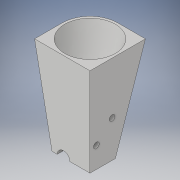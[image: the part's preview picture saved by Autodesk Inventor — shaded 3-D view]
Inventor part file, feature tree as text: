
AUTODESK INVENTOR PART (.ipt)
format: ipt  version: 2018 (Build 220112000, 112)  size: 186,368 bytes
history: native  units: in
note: dims shown in document units (in); Inventor stores cm internally (conversion verified against a paired STEP export)
features: sketch x6, loft x2, extrude x2, plane x1
ambient origin geometry x8: Origin, YZ Plane, XZ Plane, XY Plane, X Axis, Y Axis, Z Axis, Center Point
bodies: Solid1 (feature_tree)
feature tree (11):
  sketch  "Sketch1"  dims[d1=0.8in d2=1.2in]
  plane  "Work Plane1"
  loft  "Loft1"
  loft  "Loft2"
  extrude  "Extrusion1"  Depth=0.875in
  extrude  "Extrusion3"  TaperAngle=0.0deg  [1 undecoded]
  sketch  "Sketch3"  dims[d4=0.4in d5=2.8in]
  sketch  "Sketch4"  dims[d15=0.875in d17=0.875in]
  sketch  "Sketch5"  dims[d18=0.875in d19=0.0in d20=90.0deg]
  sketch  "Sketch6"  dims[d21=0.0in d22=90.0deg]
  sketch  "Sketch8"  dims[d23=1.6in d24=0.875in d26=0.875in d27=0.65in d28=0.0in d29=90.0deg d30=0.0in d31=90.0deg d32=0.4in d33=0.4in d34=0.4in d35=0.2in d36=0.0in d38=3.0in d39=0.0in d42=0.0in d43=0.25in d44=0.32in d45=0.09in d46=0.18in d47=0.2in d48=0.18in d49=0.5in d50=0.5in d51=1.0in d52=0.0in]
note: 1 required parameter value undecoded (feature->parameter linkage not recoverable at this tier; creation-order binding heuristic only, values carry confidence <= 0.55)
